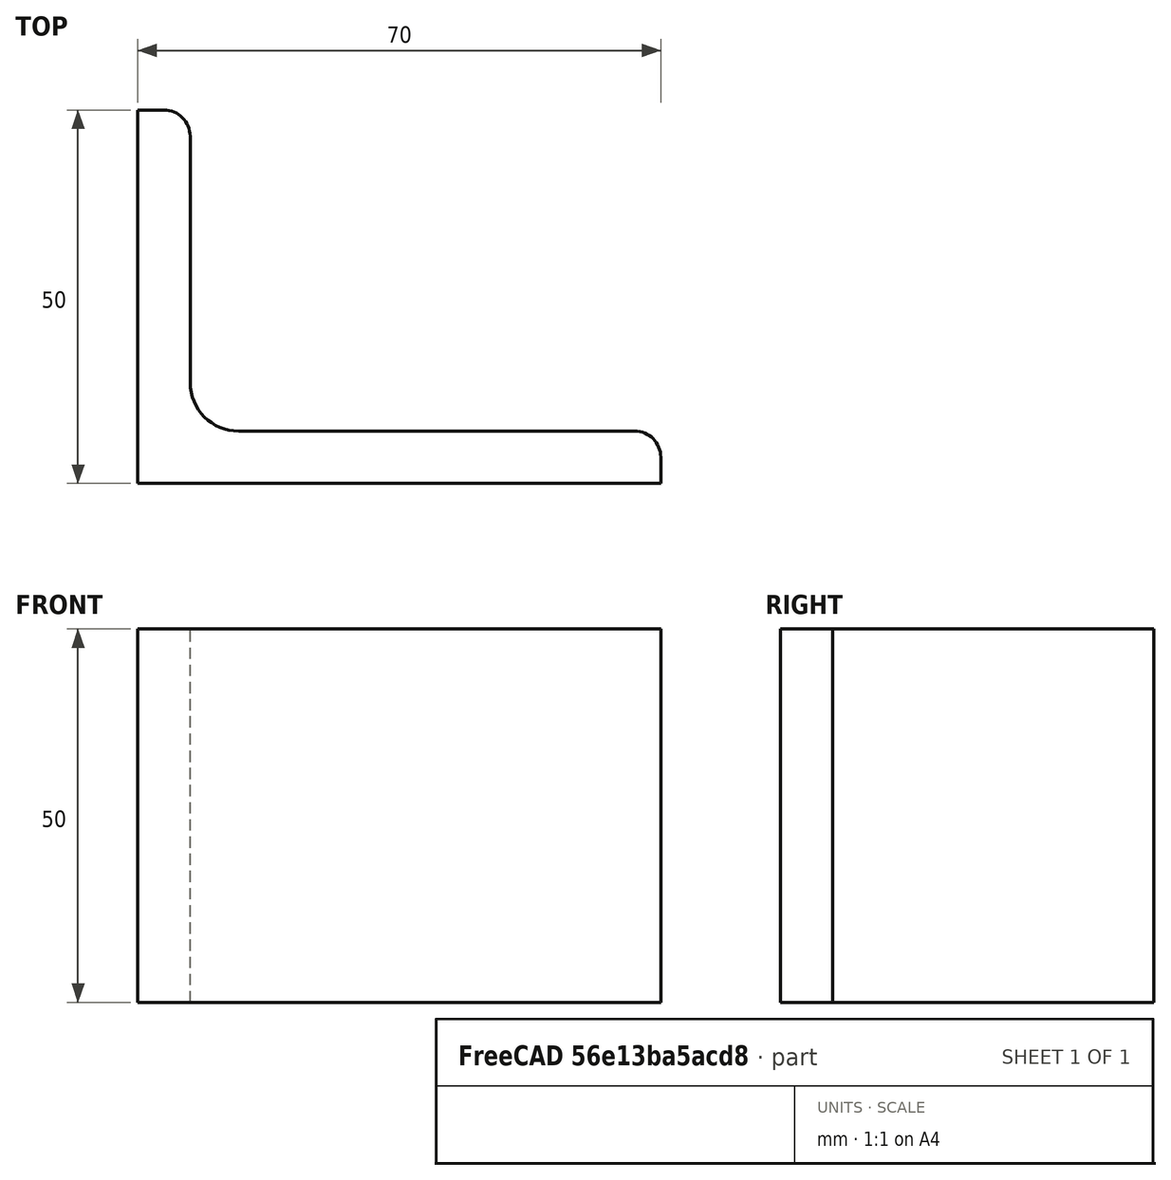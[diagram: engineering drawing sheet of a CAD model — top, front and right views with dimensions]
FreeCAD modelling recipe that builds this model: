
FCSTD DOCUMENT  (FreeCAD 0.15R4671 (Git))
Label: Angle Bar 70x50x7 EN10056 S235JR
License: All rights reserved
LicenseURL: http://en.wikipedia.org/wiki/All_rights_reserved
objects: Sketcher::SketchObject×1, Part::Extrusion×1
note: 2 computed .brp shape members not serialized (recipe doc carries the construction recipe); baked Part::Feature solids carry a one-line shape summary decoded from their .brp

FEATURE [Sketcher::SketchObject] Sketch
  sketch-geometry (9):
    g0: LineSegment StartX=0 StartY=0 StartZ=0 EndX=70 EndY=0 EndZ=0
    g1: LineSegment StartX=70 StartY=0 StartZ=0 EndX=70 EndY=3.5 EndZ=0
    g2: LineSegment StartX=66.5 StartY=7 StartZ=0 EndX=13.5 EndY=7 EndZ=0
    g3: LineSegment StartX=0 StartY=0 StartZ=0 EndX=0 EndY=50 EndZ=0
    g4: LineSegment StartX=0 StartY=50 StartZ=0 EndX=3.5 EndY=50 EndZ=0
    g5: LineSegment StartX=7 StartY=46.5 StartZ=0 EndX=7 EndY=13.5 EndZ=0
    g6: ArcOfCircle CenterX=13.5 CenterY=13.5 CenterZ=0 NormalX=0 NormalY=0 NormalZ=1 Radius=6.5 StartAngle=3.14159 EndAngle=4.71239
    g7: ArcOfCircle CenterX=3.5 CenterY=46.5 CenterZ=0 NormalX=0 NormalY=0 NormalZ=1 Radius=3.5 StartAngle=0 EndAngle=1.5708
    g8: ArcOfCircle CenterX=66.5 CenterY=3.5 CenterZ=0 NormalX=0 NormalY=0 NormalZ=1 Radius=3.5 StartAngle=0 EndAngle=1.5708
  constraints (23):
    c: Coincident(g0,g-1)
    c: Horizontal(g0)
    c: Coincident(g1,g0)
    c: Vertical(g1)
    c: Horizontal(g2)
    c: Coincident(g3,g-1)
    c: Vertical(g3)
    c: Coincident(g4,g3)
    c: Horizontal(g4)
    c: Vertical(g5)
    c: Tangent(g5,g6) = -1.5708
    c: Tangent(g2,g6) = 1.5708
    c: Tangent(g4,g7) = 1.5708
    c: Tangent(g5,g7) = 1.5708
    c: Tangent(g2,g8) = -1.5708
    c: Tangent(g1,g8) = -1.5708
    c: DistanceX(g0) = 70
    c: DistanceY(g3) = 50
    c: DistanceY(g0,g2) = 7
    c: DistanceX(g3,g5) = 7
    c: Radius(g6) = 6.5
    c: Radius(g8) = 3.5
    c: Radius(g7) = 3.5
FEATURE [Part::Extrusion] Extrude  label="Angle Bar 70x50x7 EN10056 S235JR"
  Base = -> Sketch
  Dir = (0,0,50)
  Solid = true
